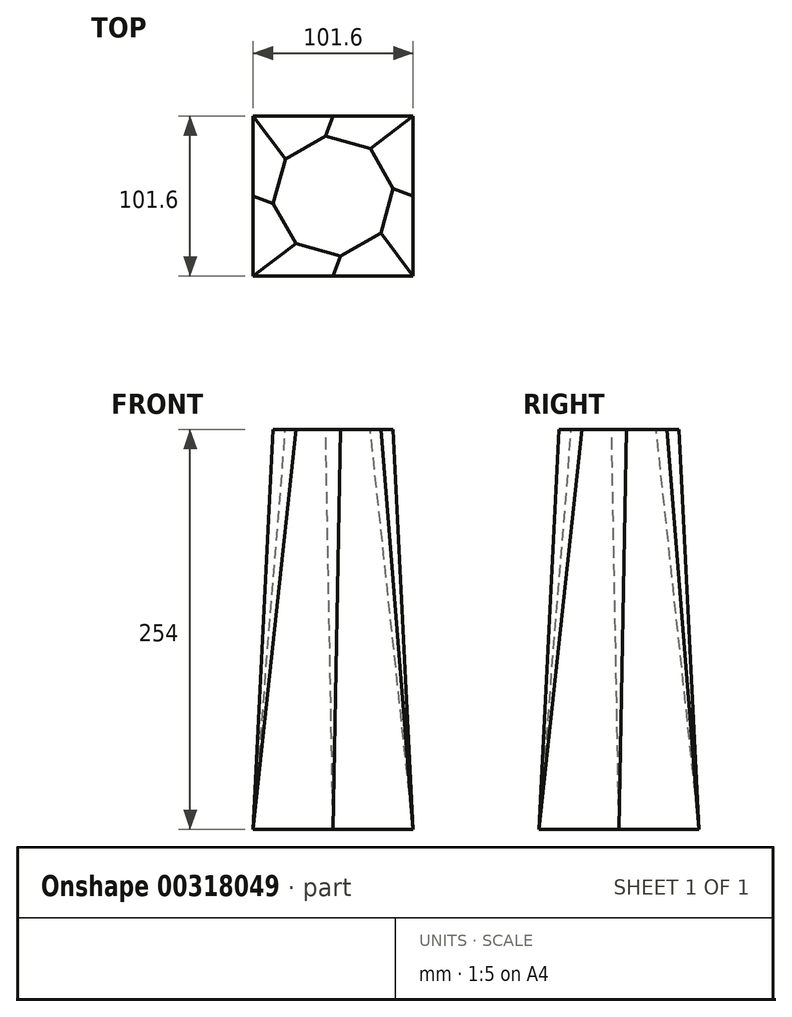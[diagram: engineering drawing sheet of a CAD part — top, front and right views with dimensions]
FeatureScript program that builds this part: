
annotation { "Feature Type Name" : "Feature", "Feature Type Description" : "" }
export const myFeature = defineFeature(function(context is Context, id is Id, definition is map)
    precondition{}
    {
        {
            var Q0;
            Q0=qCreatedBy(makeId("Top.planeOp"),FACE);
            var sketch = newSketch(context, id + "F0", { "sketchPlane" : qUnion([Q0])});
            skLineSegment(sketch, "E0.bottom", {"start": v(50.8, 50.8) * mm, "end": v(-50.8, 50.8) * mm});
            skLineSegment(sketch, "E0.top", {"start": v(50.8, -50.8) * mm, "end": v(-50.8, -50.8) * mm});
            skLineSegment(sketch, "E0.left", {"start": v(50.8, 50.8) * mm, "end": v(50.8, -50.8) * mm});
            skLineSegment(sketch, "E0.right", {"start": v(-50.8, 50.8) * mm, "end": v(-50.8, -50.8) * mm});
            skPoint(sketch, "E0.middle", {"position": v(0, 0) * mm});
            skSolve(sketch);
        }
        {
            var Q0;
            Q0=makeQuery(id+"F0.imprint","IMPRINT",FACE,{"disambiguationData":[TD([[makeQuery(id+"F0.imprint","IMPRINT",EDGE,{"derivedFrom":sQuery(id+"F0.wireOp",EDGE,"E0.bottom")}),1.0]])]});
            cPlane(context, id + "F1", {"entities" : qUnion([Q0]), "cplaneType" : CPlaneType.OFFSET, "offset" : 254 * mm, "width" : 152.4 * mm, "height" : 152.4 * mm});
        }
        {
            var Q0;
            Q0=qCreatedBy(id+"F1.planeOp",FACE);
            var sketch = newSketch(context, id + "F2", { "sketchPlane" : qUnion([Q0])});
            skCircle(sketch, "E1.cCircle", {"center": v(0, 0) * mm, "radius": 35.48 * mm, "construction": true});
            skLineSegment(sketch, "E1.0", {"start": v(23.62, 30.28) * mm, "end": v(38.11, 4.71) * mm});
            skLineSegment(sketch, "E1.1", {"start": v(38.11, 4.71) * mm, "end": v(30.28, -23.62) * mm});
            skLineSegment(sketch, "E1.2", {"start": v(30.28, -23.62) * mm, "end": v(4.71, -38.11) * mm});
            skLineSegment(sketch, "E1.3", {"start": v(4.71, -38.11) * mm, "end": v(-23.62, -30.28) * mm});
            skLineSegment(sketch, "E1.4", {"start": v(-23.62, -30.28) * mm, "end": v(-38.11, -4.71) * mm});
            skLineSegment(sketch, "E1.5", {"start": v(-38.11, -4.71) * mm, "end": v(-30.28, 23.62) * mm});
            skLineSegment(sketch, "E1.6", {"start": v(-30.28, 23.62) * mm, "end": v(-4.71, 38.11) * mm});
            skLineSegment(sketch, "E1.7", {"start": v(-4.71, 38.11) * mm, "end": v(23.62, 30.28) * mm});
            skPoint(sketch, "E1.0.midPoint", {"position": v(30.86, 17.5) * mm});
            skSolve(sketch);
        }
        {
            var Q0;
            Q0=makeQuery(id+"F0.imprint","IMPRINT",FACE,{"disambiguationData":[TD([[makeQuery(id+"F0.imprint","IMPRINT",EDGE,{"derivedFrom":sQuery(id+"F0.wireOp",EDGE,"E0.bottom")}),1.0]])]});
            var Q1;
            Q1=makeQuery(id+"F2.imprint","IMPRINT",FACE,{"disambiguationData":[TD([[makeQuery(id+"F2.imprint","IMPRINT",EDGE,{"derivedFrom":sQuery(id+"F2.wireOp",EDGE,"E1.0")}),-1.0]])]});
            loft(context, id + "F3", {"sheetProfilesArray" : [{ "sheetProfileEntities" : qUnion([Q0]) }, { "sheetProfileEntities" : qUnion([Q1]) }]});
        }
    });
